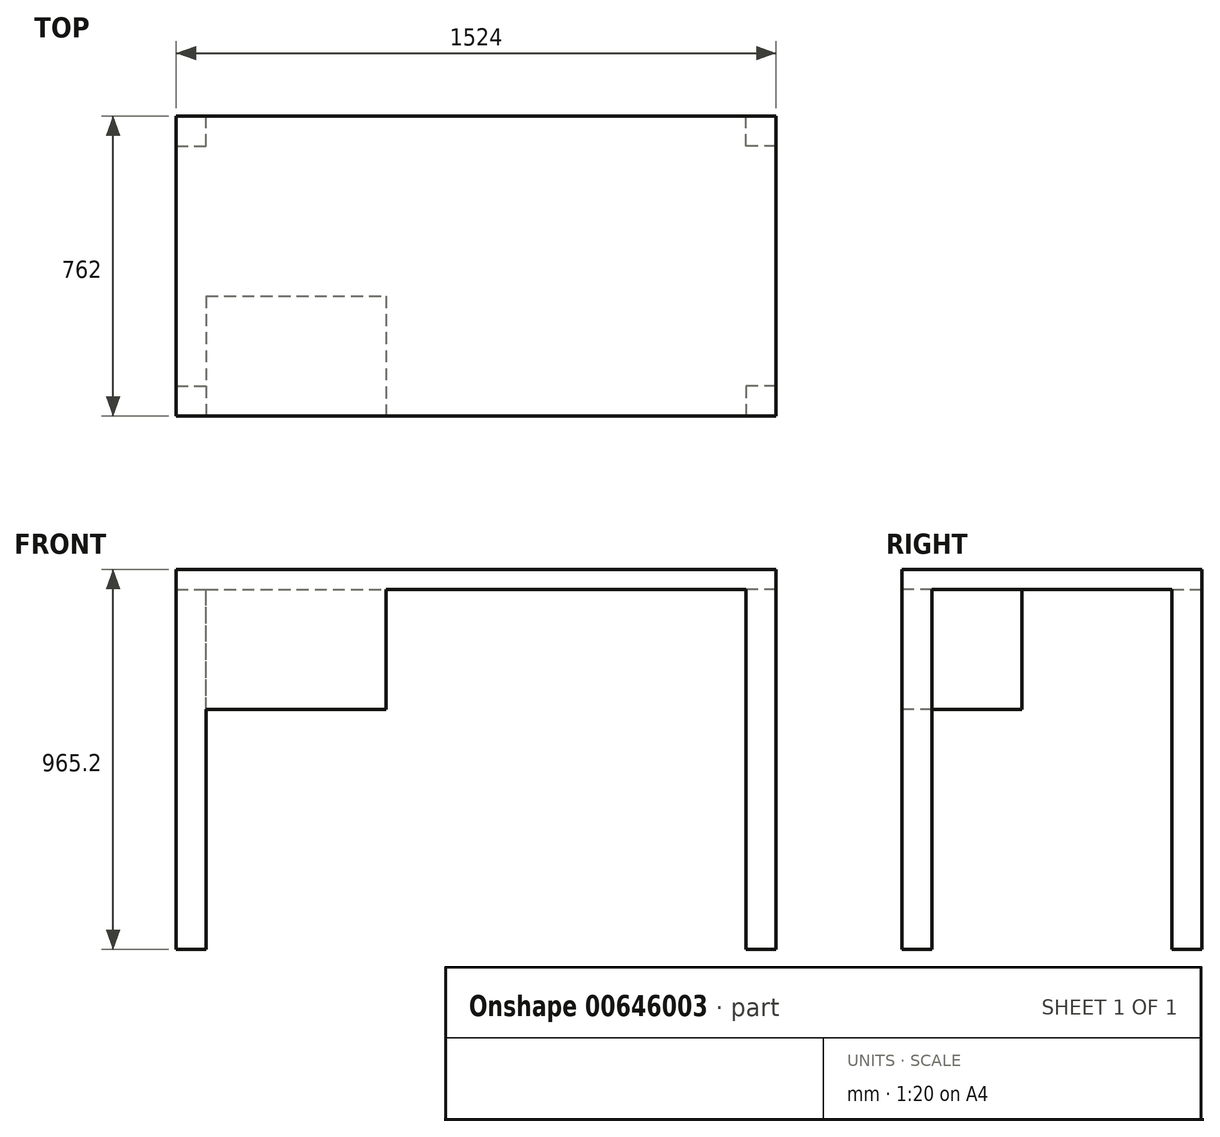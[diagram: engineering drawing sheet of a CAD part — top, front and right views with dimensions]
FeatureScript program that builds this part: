
annotation { "Feature Type Name" : "Feature", "Feature Type Description" : "" }
export const myFeature = defineFeature(function(context is Context, id is Id, definition is map)
    precondition{}
    {
        {
            var Q0;
            Q0=qCreatedBy(makeId("Top.planeOp"),FACE);
            var sketch = newSketch(context, id + "F0", { "sketchPlane" : qUnion([Q0])});
            skLineSegment(sketch, "E0.bottom", {"start": v(0, 0) * mm, "end": v(1524, 0) * mm});
            skLineSegment(sketch, "E0.top", {"start": v(0, -762) * mm, "end": v(1524, -762) * mm});
            skLineSegment(sketch, "E0.left", {"start": v(0, 0) * mm, "end": v(0, -762) * mm});
            skLineSegment(sketch, "E0.right", {"start": v(1524, 0) * mm, "end": v(1524, -762) * mm});
            skSolve(sketch);
        }
        {
            var Q0;
            Q0=makeQuery(id+"F0.imprint","IMPRINT",FACE,{"disambiguationData":[TD([[makeQuery(id+"F0.imprint","IMPRINT",EDGE,{"derivedFrom":sQuery(id+"F0.wireOp",EDGE,"E0.bottom")}),-1.0]])]});
            extrude(context, id + "F1", {"entities" : qUnion([Q0]), "oppositeDirection" : true, "depth" : 50.8 * mm, "offsetDistance" : 25.4 * mm});
        }
        {
            var Q0;
            Q0=makeQuery(id+"F1.opExtrude","CAP_FACE",FACE,{"disambiguationData":[OSD([sQuery(id+"F0.wireOp",EDGE,"E0.bottom"),sQuery(id+"F0.wireOp",EDGE,"E0.top"),sQuery(id+"F0.wireOp",EDGE,"E0.left"),sQuery(id+"F0.wireOp",EDGE,"E0.right")])],"isStart":false});
            var sketch = newSketch(context, id + "F2", { "sketchPlane" : qUnion([Q0])});
            skLineSegment(sketch, "E1", {"start": v(0, 762) * mm, "end": v(0, 685.8) * mm});
            skLineSegment(sketch, "E2", {"start": v(0, 685.8) * mm, "end": v(76.2, 685.8) * mm});
            skLineSegment(sketch, "E3", {"start": v(76.2, 685.8) * mm, "end": v(76.2, 762) * mm});
            skLineSegment(sketch, "E4", {"start": v(1524, 762) * mm, "end": v(1524, 685.8) * mm});
            skLineSegment(sketch, "E5", {"start": v(1524, 685.8) * mm, "end": v(1447.8, 685.8) * mm});
            skLineSegment(sketch, "E6", {"start": v(1447.8, 685.8) * mm, "end": v(1447.8, 762) * mm});
            skLineSegment(sketch, "E7", {"start": v(1524, 381) * mm, "end": v(0, 381) * mm, "construction": true});
            skLineSegment(sketch, "E8.MirrorCS", {"start": v(76.2, 76.2) * mm, "end": v(76.2, 0) * mm});
            skLineSegment(sketch, "E9.MirrorCS", {"start": v(0, 76.2) * mm, "end": v(76.2, 76.2) * mm});
            skLineSegment(sketch, "E10.MirrorCS", {"start": v(0, 0) * mm, "end": v(0, 76.2) * mm});
            skLineSegment(sketch, "E11.MirrorCS", {"start": v(1524, 0) * mm, "end": v(1524, 76.2) * mm});
            skLineSegment(sketch, "E12.MirrorCS", {"start": v(1524, 76.2) * mm, "end": v(1447.8, 76.2) * mm});
            skLineSegment(sketch, "E13.MirrorCS", {"start": v(1447.8, 76.2) * mm, "end": v(1447.8, 0) * mm});
            skLineSegment(sketch, "E14", {"start": v(0, 0) * mm, "end": v(76.2, 0) * mm});
            skLineSegment(sketch, "E15", {"start": v(1524, 0) * mm, "end": v(1447.8, 0) * mm});
            skLineSegment(sketch, "E16", {"start": v(0, 762) * mm, "end": v(76.2, 762) * mm});
            skLineSegment(sketch, "E17", {"start": v(1524, 762) * mm, "end": v(1447.8, 762) * mm});
            skSolve(sketch);
        }
        {
            var Q0;
            Q0=makeQuery(id+"F2.imprint","IMPRINT",FACE,{"disambiguationData":[TD([[makeQuery(id+"F2.imprint","IMPRINT",EDGE,{"derivedFrom":sQuery(id+"F2.wireOp",EDGE,"E1")}),-1.0]])]});
            var Q1;
            Q1=makeQuery(id+"F2.imprint","IMPRINT",FACE,{"disambiguationData":[TD([[makeQuery(id+"F2.imprint","IMPRINT",EDGE,{"derivedFrom":sQuery(id+"F2.wireOp",EDGE,"E8.MirrorCS")}),-1.0]])]});
            var Q2;
            Q2=makeQuery(id+"F2.imprint","IMPRINT",FACE,{"disambiguationData":[TD([[makeQuery(id+"F2.imprint","IMPRINT",EDGE,{"derivedFrom":sQuery(id+"F2.wireOp",EDGE,"E11.MirrorCS")}),1.0]])]});
            var Q3;
            Q3=makeQuery(id+"F2.imprint","IMPRINT",FACE,{"disambiguationData":[TD([[makeQuery(id+"F2.imprint","IMPRINT",EDGE,{"derivedFrom":sQuery(id+"F2.wireOp",EDGE,"E4")}),1.0]])]});
            extrude(context, id + "F3", {"entities" : qUnion([Q0, Q1, Q2, Q3]), "operationType" : NewBodyOperationType.ADD, "depth" : 914.4 * mm, "offsetDistance" : 25.4 * mm});
        }
        {
            var Q0;
            Q0=makeQuery(id+"F3.boolean.opBoolean","MERGE",FACE,{"derivedFrom":[makeQuery(id+"F1.opExtrude","SWEPT_FACE",FACE,{"disambiguationData":[OSD([sQuery(id+"F0.wireOp",EDGE,"E0.top")])]}),makeQuery(id+"F3.opExtrude","SWEPT_FACE",FACE,{"disambiguationData":[OSD([sQuery(id+"F2.wireOp",EDGE,"E16")])]}),makeQuery(id+"F3.opExtrude","SWEPT_FACE",FACE,{"disambiguationData":[OSD([sQuery(id+"F2.wireOp",EDGE,"E17")])]})]});
            var sketch = newSketch(context, id + "F4", { "sketchPlane" : qUnion([Q0])});
            skLineSegment(sketch, "E18", {"start": v(76.2, -50.8) * mm, "end": v(533.4, -50.8) * mm});
            skLineSegment(sketch, "E19", {"start": v(533.4, -50.8) * mm, "end": v(533.4, -355.6) * mm});
            skLineSegment(sketch, "E20", {"start": v(533.4, -355.6) * mm, "end": v(76.2, -355.6) * mm});
            skLineSegment(sketch, "E21", {"start": v(76.2, -355.6) * mm, "end": v(76.2, -50.8) * mm});
            skSolve(sketch);
        }
        {
            var Q0;
            Q0=makeQuery(id+"F4.imprint","IMPRINT",FACE,{"disambiguationData":[TD([[makeQuery(id+"F4.imprint","IMPRINT",EDGE,{"derivedFrom":sQuery(id+"F4.wireOp",EDGE,"E18")}),-1.0]])]});
            extrude(context, id + "F5", {"entities" : qUnion([Q0]), "operationType" : NewBodyOperationType.ADD, "oppositeDirection" : true, "depth" : 304.8 * mm, "offsetDistance" : 25.4 * mm});
        }
    });
